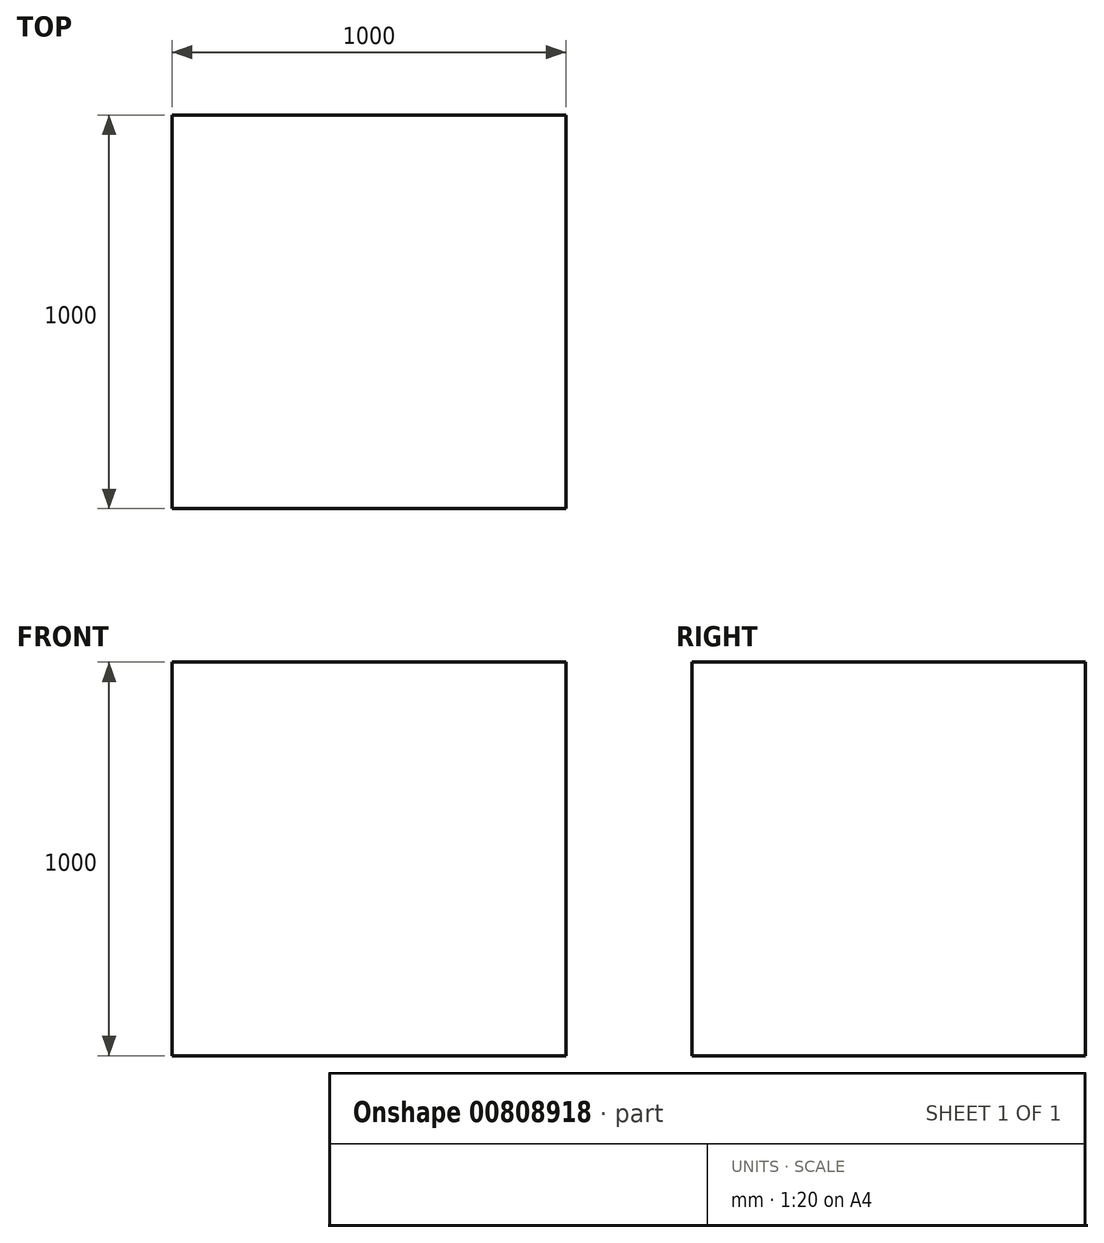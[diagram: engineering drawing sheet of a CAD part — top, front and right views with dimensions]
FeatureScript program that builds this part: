
annotation { "Feature Type Name" : "Feature", "Feature Type Description" : "" }
export const myFeature = defineFeature(function(context is Context, id is Id, definition is map)
    precondition{}
    {
        {
            var Q0;
            Q0=qCreatedBy(makeId("Front.planeOp"),FACE);
            var sketch = newSketch(context, id + "F0", { "sketchPlane" : qUnion([Q0])});
            skLineSegment(sketch, "E0", {"start": v(0, 0) * mm, "end": v(1000, 0) * mm});
            skSolve(sketch);
        }
        {
            var Q0;
            Q0=sQuery(id+"F0.wireOp",EDGE,"E0");
            extrude(context, id + "F1", {"bodyType" : ToolBodyType.SURFACE, "surfaceEntities" : qUnion([Q0]), "oppositeDirection" : true, "depth" : 1000 * mm, "offsetDistance" : 25 * mm});
        }
        {
            var Q0;
            Q0=qSketchRegion(id+"F0",true);
            var Q1;
            Q1=makeQuery(id+"F1.opExtrude","SWEPT_FACE",FACE,{"disambiguationData":[OSD([sQuery(id+"F0.wireOp",EDGE,"E0")])]});
            extrude(context, id + "F2", {"entities" : qUnion([Q0, Q1]), "depth" : 1000 * mm, "offsetDistance" : 25 * mm});
        }
    });
